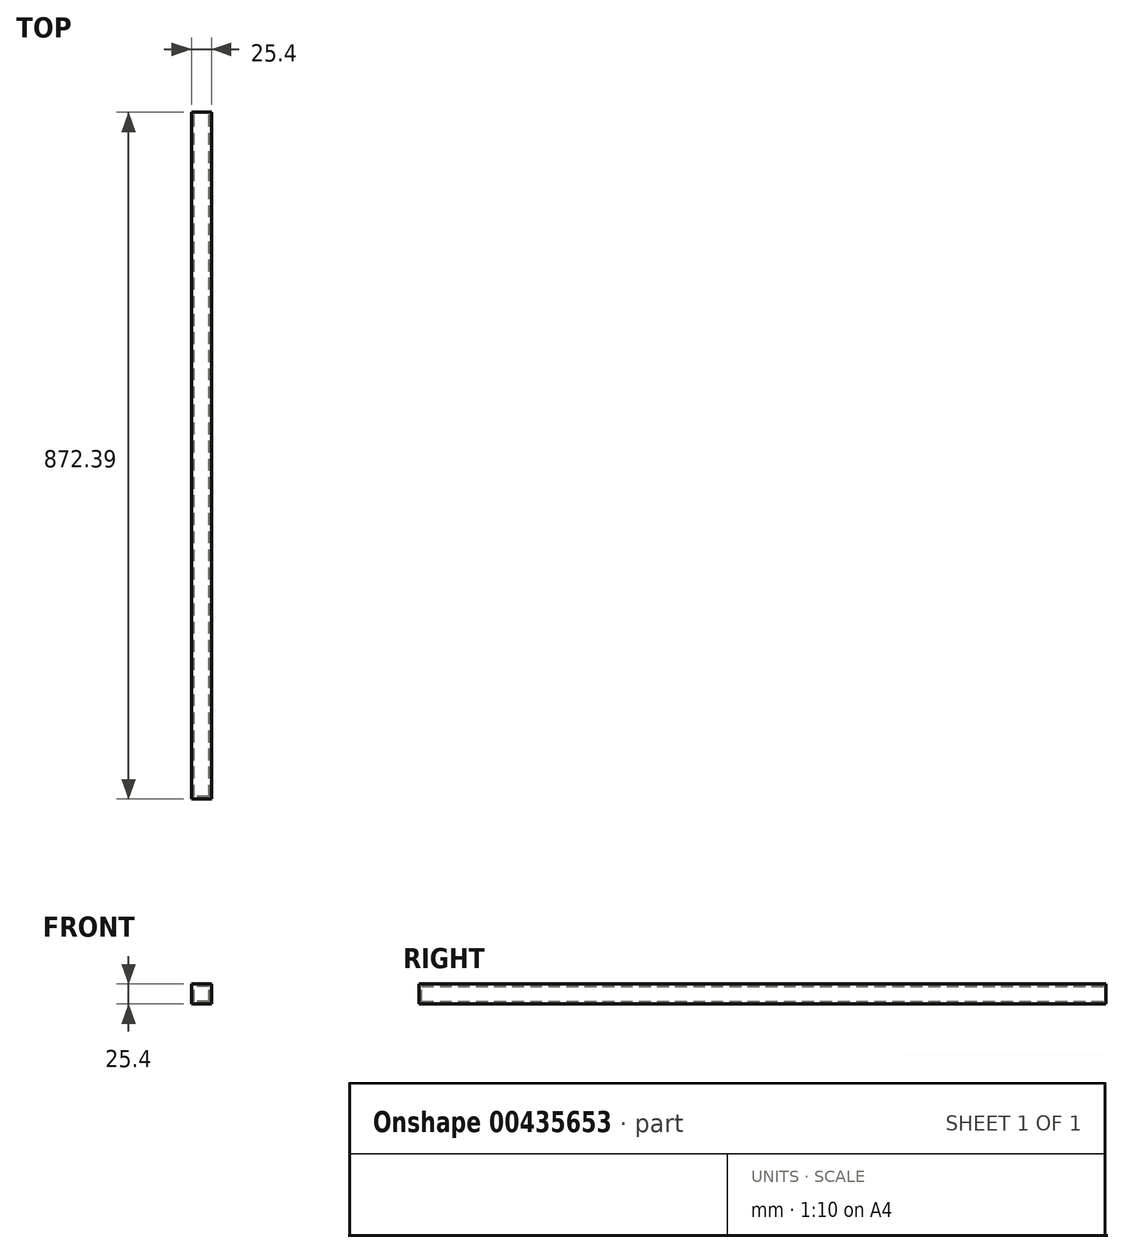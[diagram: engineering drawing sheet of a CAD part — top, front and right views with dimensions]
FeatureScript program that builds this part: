
annotation { "Feature Type Name" : "Feature", "Feature Type Description" : "" }
export const myFeature = defineFeature(function(context is Context, id is Id, definition is map)
    precondition{}
    {
        {
            var Q0;
            Q0=qCreatedBy(makeId("Front.planeOp"),FACE);
            var sketch = newSketch(context, id + "F0", { "sketchPlane" : qUnion([Q0])});
            skLineSegment(sketch, "E0.bottom", {"start": v(12.7, -12.7) * mm, "end": v(-12.7, -12.7) * mm});
            skLineSegment(sketch, "E0.top", {"start": v(12.7, 12.7) * mm, "end": v(-12.7, 12.7) * mm});
            skLineSegment(sketch, "E0.left", {"start": v(12.7, -12.7) * mm, "end": v(12.7, 12.7) * mm});
            skLineSegment(sketch, "E0.right", {"start": v(-12.7, -12.7) * mm, "end": v(-12.7, 12.7) * mm});
            skPoint(sketch, "E0.middle", {"position": v(0, 0) * mm});
            skSolve(sketch);
        }
        {
            var Q0;
            Q0=makeQuery(id+"F0.imprint","IMPRINT",FACE,{"disambiguationData":[TD([[makeQuery(id+"F0.imprint","IMPRINT",EDGE,{"derivedFrom":sQuery(id+"F0.wireOp",EDGE,"E0.bottom")}),-1.0]])]});
            extrude(context, id + "F1", {"entities" : qUnion([Q0]), "depth" : 872.4 * mm});
        }
        {
            var Q0;
            Q0=makeQuery(id+"F1.opExtrude","CAP_FACE",FACE,{"disambiguationData":[OSD([sQuery(id+"F0.wireOp",EDGE,"E0.bottom"),sQuery(id+"F0.wireOp",EDGE,"E0.top"),sQuery(id+"F0.wireOp",EDGE,"E0.left"),sQuery(id+"F0.wireOp",EDGE,"E0.right")])],"isStart":true});
            shell(context, id + "F2", {"entities" : qUnion([Q0]), "thickness" : 3.17 * mm});
        }
    });
